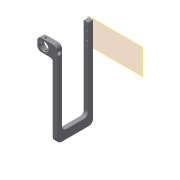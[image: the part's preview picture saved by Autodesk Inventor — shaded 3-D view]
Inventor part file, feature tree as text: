
AUTODESK INVENTOR PART (.ipt)
format: ipt  version: 2019.4 (Build 234330000, 330)  size: 196,608 bytes
history: native  units: mm
features: sketch x6, projected_geometry x6, extrude x5, reference x5, other x4, plane x1, fillet x1, pattern_circular x1, hole x1
ambient origin geometry x8: Origin, YZ Plane, XZ Plane, XY Plane, X Axis, Y Axis, Z Axis, Center Point
bodies: Solid1 (feature_tree)
feature tree (30):
  plane  "Work Plane1"
  extrude  "Extrusion1"  Depth=145.0mm
  extrude  "Extrusion2"  Depth=8.0mm
  extrude  "Extrusion3"  Depth=122.0mm
  fillet  "Fillet1"  Radius=27.0mm
  extrude  "Extrusion4"  Depth=5.0mm
  extrude  "Extrusion5"  Depth=8.0mm
  pattern_circular  "Circular Pattern1"  [2 undecoded]
  hole  "Hole1"  [1 undecoded]
  sketch  "Sketch1"  dims[d0=5.0mm d1=145.0mm]
  reference  "Reference1"
  reference  "Reference2"
  reference  "Reference3"
  reference  "Reference4"
  sketch  "Sketch2"  dims[d2=8.0mm d3=0.0mm d4=14.0mm]
  projected_geometry  "Projected Loop1"
  sketch  "Sketch3"  dims[d5=50.0mm d6=0.0mm d7=122.0mm d8=27.0mm]
  reference  "Reference5"
  projected_geometry  "Projected Loop2"
  sketch  "Sketch4"  dims[d9=20.0mm d10=5.0mm]
  projected_geometry  "Projected Loop3"
  projected_geometry  "Projected Loop4"
  sketch  "Sketch5"  dims[d11=8.0mm d12=0.0mm d13=7.0mm]
  projected_geometry  "Projected Loop5"
  sketch  "Sketch6"  dims[d14=2.0mm d15=0.0mm d16=15.0mm d17=2.8mm d18=10.0mm d19=0.0mm d20=40.0mm d21=360.0deg d23=2.8mm d24=6.0mm d25=7.0mm d26=8.0mm d27=90.0deg d28=8.0mm d29=20.594885mm]
  projected_geometry  "Projected Loop6"
  other  "Assembly_Opentrons_Imagingunit_v3.iam"
  other  "Assembly_Opentrons_Autofocus_v2:1"
  other  "01_Slide_camera_v1:1"
  other  "00_objectivelens_10x:1"
note: 3 required parameter values undecoded (feature->parameter linkage not recoverable at this tier; creation-order binding heuristic only, values carry confidence <= 0.55)
